# Revit family: MB-1101
name_source: partatom
category: Plumbing Fixtures
revit_build: Autodesk Revit 2014 (Build: 20130308_1515(x64)
units: mm (PartAtom-declared; Revit-internal decimal feet)

## types (1)
- MB-1101
    Abs Plastic = Plastic
    Aluminum Body = Aluminum
    Anodized Aluminum Finish = Aluminum, Anodized
    Container Capacity = 0.2116 gal
    Current Consumption = 160 mA
    Description = Foam Soap Dispenser, Electronic Batteries
    Detection Range = 1,57" To 2,36" Self-Adjusting
    Discharge Volume = 0.0013 gal
    Environment Temperature = 169 - 1352 °F
    Features = Infrared Sensor Automatic Activation; Type Of Deposit (Included): Reusable; Type Of Soap: Foam
    Feeding = 4 Alkaline Batteries (1.5 V)
    Feeding Voltage = 5 V
    Instructive = http://helvex.com
    Manufacturer = HELVEX
    Model = MB-1101
    Power Consumption = 1 W
    Response Time = 0,5 - 1 Seconds
    Total Depth = 4"
    Total Height = 11"
    Total Weight = 1.54 lb
    Total Width = 4"
    Type Comments = Electronic Line
    URL = http://helvex.com

## geometry (parser evidence)
native form markers: Sweep x3
no freeform markers — native parametric forms only
